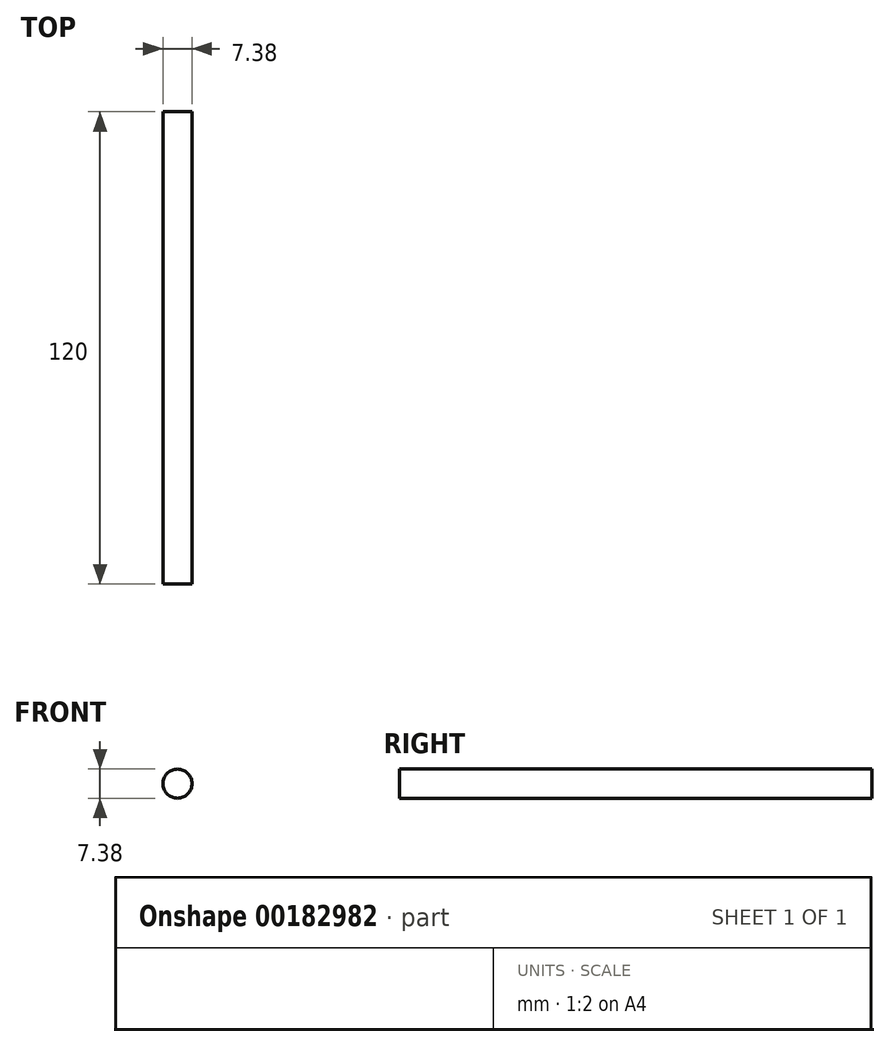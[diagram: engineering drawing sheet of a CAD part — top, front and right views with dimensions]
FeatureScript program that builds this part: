
annotation { "Feature Type Name" : "Feature", "Feature Type Description" : "" }
export const myFeature = defineFeature(function(context is Context, id is Id, definition is map)
    precondition{}
    {
        {
            var Q0;
            Q0=qCreatedBy(makeId("Front.planeOp"),FACE);
            var sketch = newSketch(context, id + "F0", { "sketchPlane" : qUnion([Q0])});
            skCircle(sketch, "E0.cCircle", {"center": v(0, 0) * mm, "radius": 6.18 * mm, "construction": true});
            skLineSegment(sketch, "E0.0", {"start": v(6.18, 3.57) * mm, "end": v(6.18, -3.57) * mm});
            skLineSegment(sketch, "E0.1", {"start": v(6.18, -3.57) * mm, "end": v(0, -7.14) * mm});
            skLineSegment(sketch, "E0.2", {"start": v(0, -7.14) * mm, "end": v(-6.18, -3.57) * mm});
            skLineSegment(sketch, "E0.3", {"start": v(-6.18, -3.57) * mm, "end": v(-6.18, 3.57) * mm});
            skLineSegment(sketch, "E0.4", {"start": v(-6.18, 3.57) * mm, "end": v(0, 7.14) * mm});
            skLineSegment(sketch, "E0.5", {"start": v(0, 7.14) * mm, "end": v(6.18, 3.57) * mm});
            skPoint(sketch, "E0.0.midPoint", {"position": v(6.18, 0) * mm});
            skCircle(sketch, "E1", {"center": v(0, 0) * mm, "radius": 3.7 * mm});
            skSolve(sketch);
        }
        {
            var Q0;
            Q0=makeQuery(id+"F0.imprint","IMPRINT",FACE,{"disambiguationData":[TD([[makeQuery(id+"F0.imprint","IMPRINT",EDGE,{"derivedFrom":sQuery(id+"F0.wireOp",EDGE,"E0.0")}),-1.0]])]});
            var Q1;
            Q1=sQuery(id+"F0.wireOp",EDGE,"E1");
            extrude(context, id + "F1", {"entities" : qUnion([Q0]), "bodyType" : ToolBodyType.SURFACE, "surfaceEntities" : qUnion([Q1]), "depth" : 120 * mm});
        }
    });
